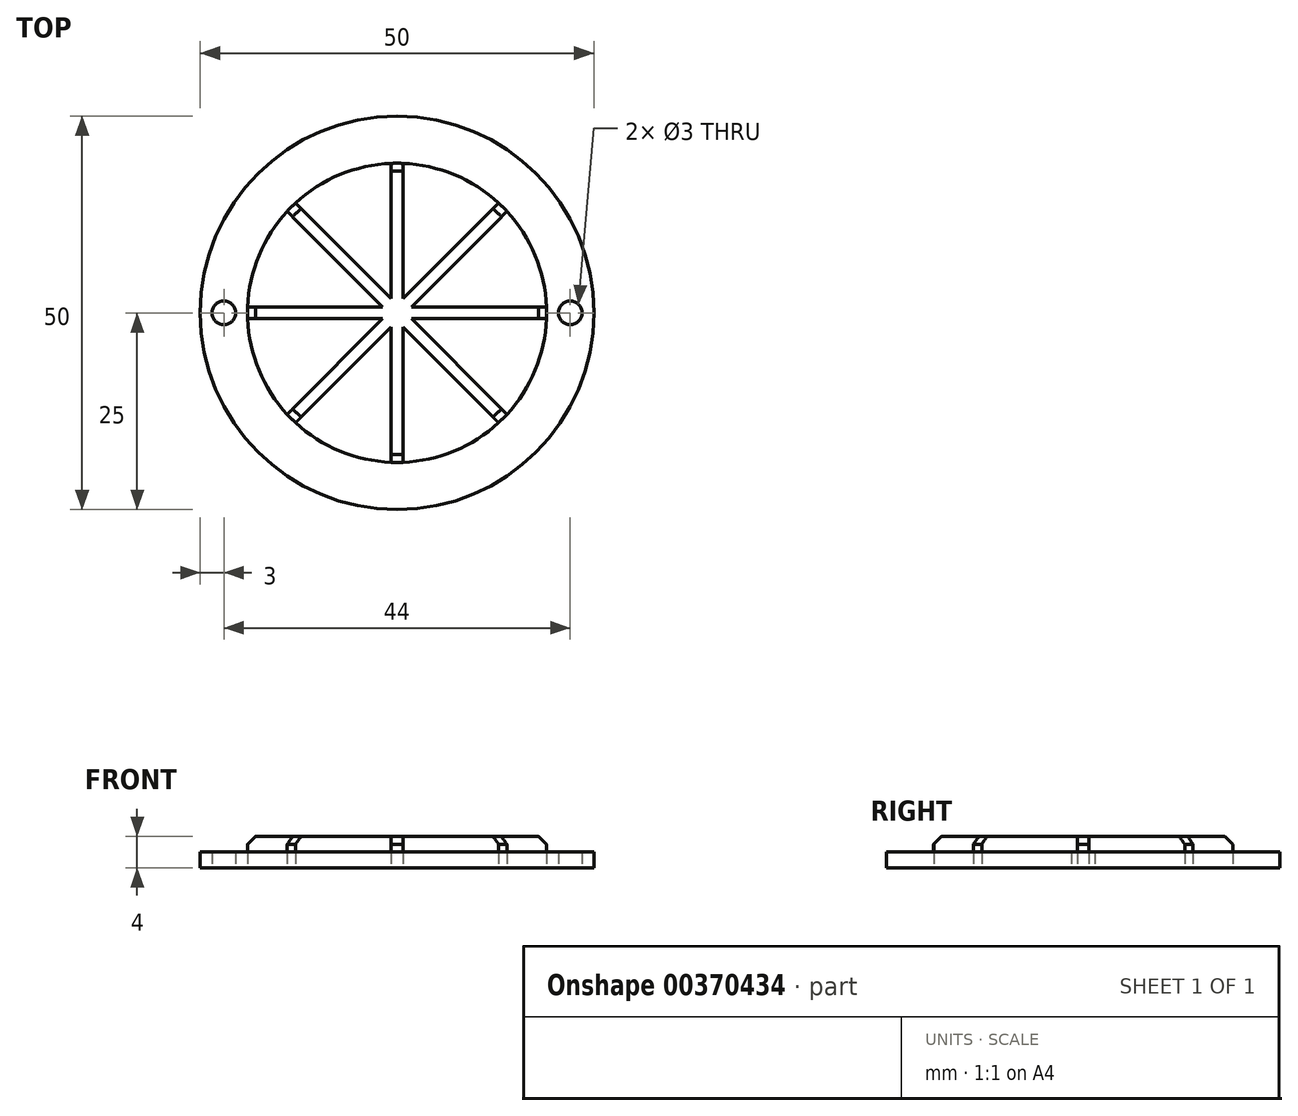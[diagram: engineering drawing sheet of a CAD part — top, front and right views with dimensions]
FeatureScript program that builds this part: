
annotation { "Feature Type Name" : "Feature", "Feature Type Description" : "" }
export const myFeature = defineFeature(function(context is Context, id is Id, definition is map)
    precondition{}
    {
        {
            var Q0;
            Q0=qCreatedBy(makeId("Top.planeOp"),FACE);
            var sketch = newSketch(context, id + "F0", { "sketchPlane" : qUnion([Q0])});
            skCircle(sketch, "E0", {"center": v(0, 0) * mm, "radius": 19 * mm});
            skCircle(sketch, "E1", {"center": v(0, 0) * mm, "radius": 25 * mm});
            skLineSegment(sketch, "E2", {"start": v(0, 0) * mm, "end": v(-19, 0) * mm});
            skLineSegment(sketch, "E3", {"start": v(0, 0) * mm, "end": v(19, 0) * mm});
            skLineSegment(sketch, "E4", {"start": v(0, 0) * mm, "end": v(0, 19) * mm});
            skLineSegment(sketch, "E5", {"start": v(0, 0) * mm, "end": v(0, -19) * mm});
            skPoint(sketch, "E6", {"position": v(-22, 0) * mm});
            skPoint(sketch, "E7", {"position": v(22, 0) * mm});
            skLineSegment(sketch, "E8", {"start": v(-18.99, 0.75) * mm, "end": v(18.99, 0.75) * mm});
            skLineSegment(sketch, "E9", {"start": v(-18.99, -0.75) * mm, "end": v(18.99, -0.75) * mm});
            skLineSegment(sketch, "E10", {"start": v(-0.75, 18.99) * mm, "end": v(-0.75, -18.99) * mm});
            skLineSegment(sketch, "E11", {"start": v(0.75, 18.99) * mm, "end": v(0.75, -18.99) * mm});
            skLineSegment(sketch, "E12", {"start": v(0, 0) * mm, "end": v(13.44, -13.44) * mm});
            skLineSegment(sketch, "E13", {"start": v(0, 0) * mm, "end": v(-13.44, 13.44) * mm});
            skLineSegment(sketch, "E14", {"start": v(0, 0) * mm, "end": v(13.44, 13.44) * mm});
            skLineSegment(sketch, "E15", {"start": v(0, 0) * mm, "end": v(-13.44, -13.44) * mm});
            skLineSegment(sketch, "E16", {"start": v(-12.9, -13.95) * mm, "end": v(13.95, 12.9) * mm});
            skLineSegment(sketch, "E17", {"start": v(-13.95, -12.9) * mm, "end": v(12.9, 13.95) * mm});
            skLineSegment(sketch, "E18", {"start": v(-12.9, 13.95) * mm, "end": v(13.95, -12.9) * mm});
            skLineSegment(sketch, "E19", {"start": v(-13.95, 12.9) * mm, "end": v(12.9, -13.95) * mm});
            skSolve(sketch);
        }
        {
            var Q0;
            {var subQ0=sQuery(id+"F0.wireOp",EDGE,"E2");var subQ1=sQuery(id+"F0.wireOp",EDGE,"E0");var subQ2=makeQuery(id+"F0.imprint","INTERSECT",VERTEX,{"derivedFrom":[subQ1,subQ0]});Q0=makeQuery(id+"F0.imprint","IMPRINT",FACE,{"disambiguationData":[TD([[makeQuery(id+"F0.imprint","IMPRINT",EDGE,{"disambiguationData":[TD([[subQ2,-1.0]])],"derivedFrom":subQ1}),1.0]])]});}
            var Q1;
            {var subQ0=sQuery(id+"F0.wireOp",EDGE,"E2");var subQ1=sQuery(id+"F0.wireOp",EDGE,"E0");var subQ2=makeQuery(id+"F0.imprint","INTERSECT",VERTEX,{"derivedFrom":[subQ1,subQ0]});Q1=makeQuery(id+"F0.imprint","IMPRINT",FACE,{"disambiguationData":[TD([[makeQuery(id+"F0.imprint","IMPRINT",EDGE,{"disambiguationData":[TD([[subQ2,1.0]])],"derivedFrom":subQ1}),1.0]])]});}
            var Q2;
            {var subQ0=sQuery(id+"F0.wireOp",EDGE,"E13");var subQ1=sQuery(id+"F0.wireOp",EDGE,"E0");var subQ2=makeQuery(id+"F0.imprint","INTERSECT",VERTEX,{"derivedFrom":[subQ1,subQ0]});Q2=makeQuery(id+"F0.imprint","IMPRINT",FACE,{"disambiguationData":[TD([[makeQuery(id+"F0.imprint","IMPRINT",EDGE,{"disambiguationData":[TD([[subQ2,-1.0]])],"derivedFrom":subQ1}),1.0]])]});}
            var Q3;
            {var subQ0=sQuery(id+"F0.wireOp",EDGE,"E13");var subQ1=sQuery(id+"F0.wireOp",EDGE,"E0");var subQ2=makeQuery(id+"F0.imprint","INTERSECT",VERTEX,{"derivedFrom":[subQ1,subQ0]});Q3=makeQuery(id+"F0.imprint","IMPRINT",FACE,{"disambiguationData":[TD([[makeQuery(id+"F0.imprint","IMPRINT",EDGE,{"disambiguationData":[TD([[subQ2,1.0]])],"derivedFrom":subQ1}),1.0]])]});}
            var Q4;
            {var subQ0=sQuery(id+"F0.wireOp",EDGE,"E4");var subQ1=sQuery(id+"F0.wireOp",EDGE,"E0");var subQ2=makeQuery(id+"F0.imprint","INTERSECT",VERTEX,{"derivedFrom":[subQ1,subQ0]});Q4=makeQuery(id+"F0.imprint","IMPRINT",FACE,{"disambiguationData":[TD([[makeQuery(id+"F0.imprint","IMPRINT",EDGE,{"disambiguationData":[TD([[subQ2,-1.0]])],"derivedFrom":subQ1}),1.0]])]});}
            var Q5;
            {var subQ0=sQuery(id+"F0.wireOp",EDGE,"E4");var subQ1=sQuery(id+"F0.wireOp",EDGE,"E0");var subQ2=makeQuery(id+"F0.imprint","INTERSECT",VERTEX,{"derivedFrom":[subQ1,subQ0]});Q5=makeQuery(id+"F0.imprint","IMPRINT",FACE,{"disambiguationData":[TD([[makeQuery(id+"F0.imprint","IMPRINT",EDGE,{"disambiguationData":[TD([[subQ2,1.0]])],"derivedFrom":subQ1}),1.0]])]});}
            var Q6;
            {var subQ0=sQuery(id+"F0.wireOp",EDGE,"E14");var subQ1=sQuery(id+"F0.wireOp",EDGE,"E0");var subQ2=makeQuery(id+"F0.imprint","INTERSECT",VERTEX,{"derivedFrom":[subQ1,subQ0]});Q6=makeQuery(id+"F0.imprint","IMPRINT",FACE,{"disambiguationData":[TD([[makeQuery(id+"F0.imprint","IMPRINT",EDGE,{"disambiguationData":[TD([[subQ2,-1.0]])],"derivedFrom":subQ1}),1.0]])]});}
            var Q7;
            {var subQ0=sQuery(id+"F0.wireOp",EDGE,"E14");var subQ1=sQuery(id+"F0.wireOp",EDGE,"E0");var subQ2=makeQuery(id+"F0.imprint","INTERSECT",VERTEX,{"derivedFrom":[subQ1,subQ0]});Q7=makeQuery(id+"F0.imprint","IMPRINT",FACE,{"disambiguationData":[TD([[makeQuery(id+"F0.imprint","IMPRINT",EDGE,{"disambiguationData":[TD([[subQ2,1.0]])],"derivedFrom":subQ1}),1.0]])]});}
            var Q8;
            {var subQ0=sQuery(id+"F0.wireOp",EDGE,"E3");var subQ1=sQuery(id+"F0.wireOp",EDGE,"E0");var subQ2=makeQuery(id+"F0.imprint","INTERSECT",VERTEX,{"derivedFrom":[subQ1,subQ0]});Q8=makeQuery(id+"F0.imprint","IMPRINT",FACE,{"disambiguationData":[TD([[makeQuery(id+"F0.imprint","IMPRINT",EDGE,{"disambiguationData":[TD([[subQ2,-1.0]])],"derivedFrom":subQ1}),1.0]])]});}
            var Q9;
            {var subQ0=sQuery(id+"F0.wireOp",EDGE,"E3");var subQ1=sQuery(id+"F0.wireOp",EDGE,"E0");var subQ2=makeQuery(id+"F0.imprint","INTERSECT",VERTEX,{"derivedFrom":[subQ1,subQ0]});Q9=makeQuery(id+"F0.imprint","IMPRINT",FACE,{"disambiguationData":[TD([[makeQuery(id+"F0.imprint","IMPRINT",EDGE,{"disambiguationData":[TD([[subQ2,1.0]])],"derivedFrom":subQ1}),1.0]])]});}
            var Q10;
            {var subQ0=sQuery(id+"F0.wireOp",EDGE,"E12");var subQ1=sQuery(id+"F0.wireOp",EDGE,"E0");var subQ2=makeQuery(id+"F0.imprint","INTERSECT",VERTEX,{"derivedFrom":[subQ1,subQ0]});Q10=makeQuery(id+"F0.imprint","IMPRINT",FACE,{"disambiguationData":[TD([[makeQuery(id+"F0.imprint","IMPRINT",EDGE,{"disambiguationData":[TD([[subQ2,-1.0]])],"derivedFrom":subQ1}),1.0]])]});}
            var Q11;
            {var subQ0=sQuery(id+"F0.wireOp",EDGE,"E12");var subQ1=sQuery(id+"F0.wireOp",EDGE,"E0");var subQ2=makeQuery(id+"F0.imprint","INTERSECT",VERTEX,{"derivedFrom":[subQ1,subQ0]});Q11=makeQuery(id+"F0.imprint","IMPRINT",FACE,{"disambiguationData":[TD([[makeQuery(id+"F0.imprint","IMPRINT",EDGE,{"disambiguationData":[TD([[subQ2,1.0]])],"derivedFrom":subQ1}),1.0]])]});}
            var Q12;
            {var subQ0=sQuery(id+"F0.wireOp",EDGE,"E5");var subQ1=sQuery(id+"F0.wireOp",EDGE,"E0");var subQ2=makeQuery(id+"F0.imprint","INTERSECT",VERTEX,{"derivedFrom":[subQ1,subQ0]});Q12=makeQuery(id+"F0.imprint","IMPRINT",FACE,{"disambiguationData":[TD([[makeQuery(id+"F0.imprint","IMPRINT",EDGE,{"disambiguationData":[TD([[subQ2,-1.0]])],"derivedFrom":subQ1}),1.0]])]});}
            var Q13;
            {var subQ0=sQuery(id+"F0.wireOp",EDGE,"E5");var subQ1=sQuery(id+"F0.wireOp",EDGE,"E0");var subQ2=makeQuery(id+"F0.imprint","INTERSECT",VERTEX,{"derivedFrom":[subQ1,subQ0]});Q13=makeQuery(id+"F0.imprint","IMPRINT",FACE,{"disambiguationData":[TD([[makeQuery(id+"F0.imprint","IMPRINT",EDGE,{"disambiguationData":[TD([[subQ2,1.0]])],"derivedFrom":subQ1}),1.0]])]});}
            var Q14;
            {var subQ0=sQuery(id+"F0.wireOp",EDGE,"E15");var subQ1=sQuery(id+"F0.wireOp",EDGE,"E0");var subQ2=makeQuery(id+"F0.imprint","INTERSECT",VERTEX,{"derivedFrom":[subQ1,subQ0]});Q14=makeQuery(id+"F0.imprint","IMPRINT",FACE,{"disambiguationData":[TD([[makeQuery(id+"F0.imprint","IMPRINT",EDGE,{"disambiguationData":[TD([[subQ2,-1.0]])],"derivedFrom":subQ1}),1.0]])]});}
            var Q15;
            {var subQ0=sQuery(id+"F0.wireOp",EDGE,"E15");var subQ1=sQuery(id+"F0.wireOp",EDGE,"E0");var subQ2=makeQuery(id+"F0.imprint","INTERSECT",VERTEX,{"derivedFrom":[subQ1,subQ0]});Q15=makeQuery(id+"F0.imprint","IMPRINT",FACE,{"disambiguationData":[TD([[makeQuery(id+"F0.imprint","IMPRINT",EDGE,{"disambiguationData":[TD([[subQ2,1.0]])],"derivedFrom":subQ1}),1.0]])]});}
            var Q16;
            {var subQ0=sQuery(id+"F0.wireOp",EDGE,"E17");var subQ1=sQuery(id+"F0.wireOp",EDGE,"E9");var subQ2=makeQuery(id+"F0.imprint","INTERSECT",VERTEX,{"derivedFrom":[subQ1,subQ0]});Q16=makeQuery(id+"F0.imprint","IMPRINT",FACE,{"disambiguationData":[TD([[makeQuery(id+"F0.imprint","IMPRINT",EDGE,{"disambiguationData":[TD([[subQ2,-1.0]])],"derivedFrom":subQ1}),1.0]])]});}
            var Q17;
            {var subQ0=sQuery(id+"F0.wireOp",EDGE,"E19");var subQ1=sQuery(id+"F0.wireOp",EDGE,"E9");var subQ2=makeQuery(id+"F0.imprint","INTERSECT",VERTEX,{"derivedFrom":[subQ1,subQ0]});Q17=makeQuery(id+"F0.imprint","IMPRINT",FACE,{"disambiguationData":[TD([[makeQuery(id+"F0.imprint","IMPRINT",EDGE,{"disambiguationData":[TD([[subQ2,1.0]])],"derivedFrom":subQ1}),-1.0]])]});}
            var Q18;
            {var subQ0=sQuery(id+"F0.wireOp",EDGE,"E16");var subQ1=sQuery(id+"F0.wireOp",EDGE,"E9");var subQ2=makeQuery(id+"F0.imprint","INTERSECT",VERTEX,{"derivedFrom":[subQ1,subQ0]});Q18=makeQuery(id+"F0.imprint","IMPRINT",FACE,{"disambiguationData":[TD([[makeQuery(id+"F0.imprint","IMPRINT",EDGE,{"disambiguationData":[TD([[subQ2,-1.0]])],"derivedFrom":subQ1}),-1.0]])]});}
            var Q19;
            {var subQ0=sQuery(id+"F0.wireOp",EDGE,"E18");var subQ1=sQuery(id+"F0.wireOp",EDGE,"E9");var subQ2=makeQuery(id+"F0.imprint","INTERSECT",VERTEX,{"derivedFrom":[subQ1,subQ0]});Q19=makeQuery(id+"F0.imprint","IMPRINT",FACE,{"disambiguationData":[TD([[makeQuery(id+"F0.imprint","IMPRINT",EDGE,{"disambiguationData":[TD([[subQ2,1.0]])],"derivedFrom":subQ1}),1.0]])]});}
            var Q20;
            {var subQ0=sQuery(id+"F0.wireOp",EDGE,"E16");var subQ1=sQuery(id+"F0.wireOp",EDGE,"E11");var subQ2=makeQuery(id+"F0.imprint","INTERSECT",VERTEX,{"derivedFrom":[subQ1,subQ0]});Q20=makeQuery(id+"F0.imprint","IMPRINT",FACE,{"disambiguationData":[TD([[makeQuery(id+"F0.imprint","IMPRINT",EDGE,{"disambiguationData":[TD([[subQ2,1.0]])],"derivedFrom":subQ0}),-1.0]])]});}
            var Q21;
            {var subQ0=sQuery(id+"F0.wireOp",EDGE,"E16");var subQ1=sQuery(id+"F0.wireOp",EDGE,"E9");var subQ2=makeQuery(id+"F0.imprint","INTERSECT",VERTEX,{"derivedFrom":[subQ1,subQ0]});Q21=makeQuery(id+"F0.imprint","IMPRINT",FACE,{"disambiguationData":[TD([[makeQuery(id+"F0.imprint","IMPRINT",EDGE,{"disambiguationData":[TD([[subQ2,-1.0]])],"derivedFrom":subQ0}),-1.0]])]});}
            var Q22;
            {var subQ0=sQuery(id+"F0.wireOp",EDGE,"E9");var subQ1=sQuery(id+"F0.wireOp",EDGE,"E5");var subQ2=makeQuery(id+"F0.imprint","INTERSECT",VERTEX,{"derivedFrom":[subQ1,subQ0]});Q22=makeQuery(id+"F0.imprint","IMPRINT",FACE,{"disambiguationData":[TD([[makeQuery(id+"F0.imprint","IMPRINT",EDGE,{"disambiguationData":[TD([[subQ2,-1.0]])],"derivedFrom":subQ0}),-1.0]])]});}
            var Q23;
            {var subQ0=sQuery(id+"F0.wireOp",EDGE,"E9");var subQ1=sQuery(id+"F0.wireOp",EDGE,"E5");var subQ2=makeQuery(id+"F0.imprint","INTERSECT",VERTEX,{"derivedFrom":[subQ1,subQ0]});Q23=makeQuery(id+"F0.imprint","IMPRINT",FACE,{"disambiguationData":[TD([[makeQuery(id+"F0.imprint","IMPRINT",EDGE,{"disambiguationData":[TD([[subQ2,1.0]])],"derivedFrom":subQ0}),-1.0]])]});}
            var Q24;
            {var subQ1=sQuery(id+"F0.wireOp",EDGE,"E5");var subQ3=sQuery(id+"F0.wireOp",EDGE,"E9");var subQ4=makeQuery(id+"F0.imprint","INTERSECT",VERTEX,{"derivedFrom":[subQ1,subQ3]});Q24=makeQuery(id+"F0.imprint","IMPRINT",FACE,{"disambiguationData":[TD([[makeQuery(id+"F0.imprint","IMPRINT",EDGE,{"disambiguationData":[TD([[subQ4,1.0]])],"derivedFrom":subQ3}),1.0]])]});}
            var Q25;
            {var subQ0=sQuery(id+"F0.wireOp",EDGE,"E19");var subQ1=sQuery(id+"F0.wireOp",EDGE,"E9");var subQ2=makeQuery(id+"F0.imprint","INTERSECT",VERTEX,{"derivedFrom":[subQ1,subQ0]});Q25=makeQuery(id+"F0.imprint","IMPRINT",FACE,{"disambiguationData":[TD([[makeQuery(id+"F0.imprint","IMPRINT",EDGE,{"disambiguationData":[TD([[subQ2,1.0]])],"derivedFrom":subQ0}),-1.0]])]});}
            var Q26;
            {var subQ0=sQuery(id+"F0.wireOp",EDGE,"E19");var subQ1=sQuery(id+"F0.wireOp",EDGE,"E10");var subQ2=makeQuery(id+"F0.imprint","INTERSECT",VERTEX,{"derivedFrom":[subQ1,subQ0]});Q26=makeQuery(id+"F0.imprint","IMPRINT",FACE,{"disambiguationData":[TD([[makeQuery(id+"F0.imprint","IMPRINT",EDGE,{"disambiguationData":[TD([[subQ2,-1.0]])],"derivedFrom":subQ0}),-1.0]])]});}
            var Q27;
            {var subQ1=sQuery(id+"F0.wireOp",EDGE,"E2");var subQ3=sQuery(id+"F0.wireOp",EDGE,"E10");var subQ4=makeQuery(id+"F0.imprint","INTERSECT",VERTEX,{"derivedFrom":[subQ1,subQ3]});Q27=makeQuery(id+"F0.imprint","IMPRINT",FACE,{"disambiguationData":[TD([[makeQuery(id+"F0.imprint","IMPRINT",EDGE,{"disambiguationData":[TD([[subQ4,-1.0]])],"derivedFrom":subQ3}),1.0]])]});}
            var Q28;
            {var subQ0=sQuery(id+"F0.wireOp",EDGE,"E10");var subQ1=sQuery(id+"F0.wireOp",EDGE,"E2");var subQ2=makeQuery(id+"F0.imprint","INTERSECT",VERTEX,{"derivedFrom":[subQ1,subQ0]});Q28=makeQuery(id+"F0.imprint","IMPRINT",FACE,{"disambiguationData":[TD([[makeQuery(id+"F0.imprint","IMPRINT",EDGE,{"disambiguationData":[TD([[subQ2,-1.0]])],"derivedFrom":subQ0}),-1.0]])]});}
            var Q29;
            {var subQ0=sQuery(id+"F0.wireOp",EDGE,"E10");var subQ1=sQuery(id+"F0.wireOp",EDGE,"E2");var subQ2=makeQuery(id+"F0.imprint","INTERSECT",VERTEX,{"derivedFrom":[subQ1,subQ0]});Q29=makeQuery(id+"F0.imprint","IMPRINT",FACE,{"disambiguationData":[TD([[makeQuery(id+"F0.imprint","IMPRINT",EDGE,{"disambiguationData":[TD([[subQ2,1.0]])],"derivedFrom":subQ0}),-1.0]])]});}
            var Q30;
            {var subQ0=sQuery(id+"F0.wireOp",EDGE,"E19");var subQ1=sQuery(id+"F0.wireOp",EDGE,"E8");var subQ2=makeQuery(id+"F0.imprint","INTERSECT",VERTEX,{"derivedFrom":[subQ1,subQ0]});Q30=makeQuery(id+"F0.imprint","IMPRINT",FACE,{"disambiguationData":[TD([[makeQuery(id+"F0.imprint","IMPRINT",EDGE,{"disambiguationData":[TD([[subQ2,-1.0]])],"derivedFrom":subQ1}),-1.0]])]});}
            var Q31;
            {var subQ1=sQuery(id+"F0.wireOp",EDGE,"E2");var subQ3=sQuery(id+"F0.wireOp",EDGE,"E10");var subQ4=makeQuery(id+"F0.imprint","INTERSECT",VERTEX,{"derivedFrom":[subQ1,subQ3]});Q31=makeQuery(id+"F0.imprint","IMPRINT",FACE,{"disambiguationData":[TD([[makeQuery(id+"F0.imprint","IMPRINT",EDGE,{"disambiguationData":[TD([[subQ4,1.0]])],"derivedFrom":subQ3}),1.0]])]});}
            var Q32;
            {var subQ0=sQuery(id+"F0.wireOp",EDGE,"E17");var subQ1=sQuery(id+"F0.wireOp",EDGE,"E10");var subQ2=makeQuery(id+"F0.imprint","INTERSECT",VERTEX,{"derivedFrom":[subQ1,subQ0]});Q32=makeQuery(id+"F0.imprint","IMPRINT",FACE,{"disambiguationData":[TD([[makeQuery(id+"F0.imprint","IMPRINT",EDGE,{"disambiguationData":[TD([[subQ2,-1.0]])],"derivedFrom":subQ0}),1.0]])]});}
            var Q33;
            {var subQ0=sQuery(id+"F0.wireOp",EDGE,"E17");var subQ1=sQuery(id+"F0.wireOp",EDGE,"E8");var subQ2=makeQuery(id+"F0.imprint","INTERSECT",VERTEX,{"derivedFrom":[subQ1,subQ0]});Q33=makeQuery(id+"F0.imprint","IMPRINT",FACE,{"disambiguationData":[TD([[makeQuery(id+"F0.imprint","IMPRINT",EDGE,{"disambiguationData":[TD([[subQ2,1.0]])],"derivedFrom":subQ1}),1.0]])]});}
            var Q34;
            {var subQ0=sQuery(id+"F0.wireOp",EDGE,"E17");var subQ1=sQuery(id+"F0.wireOp",EDGE,"E8");var subQ2=makeQuery(id+"F0.imprint","INTERSECT",VERTEX,{"derivedFrom":[subQ1,subQ0]});Q34=makeQuery(id+"F0.imprint","IMPRINT",FACE,{"disambiguationData":[TD([[makeQuery(id+"F0.imprint","IMPRINT",EDGE,{"disambiguationData":[TD([[subQ2,1.0]])],"derivedFrom":subQ0}),1.0]])]});}
            var Q35;
            {var subQ1=sQuery(id+"F0.wireOp",EDGE,"E4");var subQ3=sQuery(id+"F0.wireOp",EDGE,"E8");var subQ4=makeQuery(id+"F0.imprint","INTERSECT",VERTEX,{"derivedFrom":[subQ1,subQ3]});Q35=makeQuery(id+"F0.imprint","IMPRINT",FACE,{"disambiguationData":[TD([[makeQuery(id+"F0.imprint","IMPRINT",EDGE,{"disambiguationData":[TD([[subQ4,1.0]])],"derivedFrom":subQ3}),-1.0]])]});}
            var Q36;
            {var subQ0=sQuery(id+"F0.wireOp",EDGE,"E8");var subQ1=sQuery(id+"F0.wireOp",EDGE,"E4");var subQ2=makeQuery(id+"F0.imprint","INTERSECT",VERTEX,{"derivedFrom":[subQ1,subQ0]});Q36=makeQuery(id+"F0.imprint","IMPRINT",FACE,{"disambiguationData":[TD([[makeQuery(id+"F0.imprint","IMPRINT",EDGE,{"disambiguationData":[TD([[subQ2,1.0]])],"derivedFrom":subQ0}),1.0]])]});}
            var Q37;
            {var subQ0=sQuery(id+"F0.wireOp",EDGE,"E18");var subQ1=sQuery(id+"F0.wireOp",EDGE,"E8");var subQ2=makeQuery(id+"F0.imprint","INTERSECT",VERTEX,{"derivedFrom":[subQ1,subQ0]});Q37=makeQuery(id+"F0.imprint","IMPRINT",FACE,{"disambiguationData":[TD([[makeQuery(id+"F0.imprint","IMPRINT",EDGE,{"disambiguationData":[TD([[subQ2,-1.0]])],"derivedFrom":subQ1}),1.0]])]});}
            var Q38;
            {var subQ0=sQuery(id+"F0.wireOp",EDGE,"E8");var subQ1=sQuery(id+"F0.wireOp",EDGE,"E4");var subQ2=makeQuery(id+"F0.imprint","INTERSECT",VERTEX,{"derivedFrom":[subQ1,subQ0]});Q38=makeQuery(id+"F0.imprint","IMPRINT",FACE,{"disambiguationData":[TD([[makeQuery(id+"F0.imprint","IMPRINT",EDGE,{"disambiguationData":[TD([[subQ2,-1.0]])],"derivedFrom":subQ0}),1.0]])]});}
            var Q39;
            {var subQ0=sQuery(id+"F0.wireOp",EDGE,"E18");var subQ1=sQuery(id+"F0.wireOp",EDGE,"E8");var subQ2=makeQuery(id+"F0.imprint","INTERSECT",VERTEX,{"derivedFrom":[subQ1,subQ0]});Q39=makeQuery(id+"F0.imprint","IMPRINT",FACE,{"disambiguationData":[TD([[makeQuery(id+"F0.imprint","IMPRINT",EDGE,{"disambiguationData":[TD([[subQ2,-1.0]])],"derivedFrom":subQ0}),1.0]])]});}
            var Q40;
            {var subQ0=sQuery(id+"F0.wireOp",EDGE,"E18");var subQ1=sQuery(id+"F0.wireOp",EDGE,"E11");var subQ2=makeQuery(id+"F0.imprint","INTERSECT",VERTEX,{"derivedFrom":[subQ1,subQ0]});Q40=makeQuery(id+"F0.imprint","IMPRINT",FACE,{"disambiguationData":[TD([[makeQuery(id+"F0.imprint","IMPRINT",EDGE,{"disambiguationData":[TD([[subQ2,1.0]])],"derivedFrom":subQ0}),1.0]])]});}
            var Q41;
            {var subQ0=sQuery(id+"F0.wireOp",EDGE,"E16");var subQ1=sQuery(id+"F0.wireOp",EDGE,"E8");var subQ2=makeQuery(id+"F0.imprint","INTERSECT",VERTEX,{"derivedFrom":[subQ1,subQ0]});Q41=makeQuery(id+"F0.imprint","IMPRINT",FACE,{"disambiguationData":[TD([[makeQuery(id+"F0.imprint","IMPRINT",EDGE,{"disambiguationData":[TD([[subQ2,1.0]])],"derivedFrom":subQ1}),-1.0]])]});}
            var Q42;
            {var subQ0=sQuery(id+"F0.wireOp",EDGE,"E11");var subQ1=sQuery(id+"F0.wireOp",EDGE,"E3");var subQ2=makeQuery(id+"F0.imprint","INTERSECT",VERTEX,{"derivedFrom":[subQ1,subQ0]});Q42=makeQuery(id+"F0.imprint","IMPRINT",FACE,{"disambiguationData":[TD([[makeQuery(id+"F0.imprint","IMPRINT",EDGE,{"disambiguationData":[TD([[subQ2,1.0]])],"derivedFrom":subQ0}),1.0]])]});}
            var Q43;
            {var subQ1=sQuery(id+"F0.wireOp",EDGE,"E3");var subQ3=sQuery(id+"F0.wireOp",EDGE,"E11");var subQ4=makeQuery(id+"F0.imprint","INTERSECT",VERTEX,{"derivedFrom":[subQ1,subQ3]});Q43=makeQuery(id+"F0.imprint","IMPRINT",FACE,{"disambiguationData":[TD([[makeQuery(id+"F0.imprint","IMPRINT",EDGE,{"disambiguationData":[TD([[subQ4,-1.0]])],"derivedFrom":subQ3}),-1.0]])]});}
            var Q44;
            {var subQ1=sQuery(id+"F0.wireOp",EDGE,"E5");var subQ3=sQuery(id+"F0.wireOp",EDGE,"E9");var subQ4=makeQuery(id+"F0.imprint","INTERSECT",VERTEX,{"derivedFrom":[subQ1,subQ3]});Q44=makeQuery(id+"F0.imprint","IMPRINT",FACE,{"disambiguationData":[TD([[makeQuery(id+"F0.imprint","IMPRINT",EDGE,{"disambiguationData":[TD([[subQ4,-1.0]])],"derivedFrom":subQ3}),1.0]])]});}
            var Q45;
            {var subQ1=sQuery(id+"F0.wireOp",EDGE,"E3");var subQ3=sQuery(id+"F0.wireOp",EDGE,"E11");var subQ4=makeQuery(id+"F0.imprint","INTERSECT",VERTEX,{"derivedFrom":[subQ1,subQ3]});Q45=makeQuery(id+"F0.imprint","IMPRINT",FACE,{"disambiguationData":[TD([[makeQuery(id+"F0.imprint","IMPRINT",EDGE,{"disambiguationData":[TD([[subQ4,1.0]])],"derivedFrom":subQ3}),-1.0]])]});}
            var Q46;
            {var subQ1=sQuery(id+"F0.wireOp",EDGE,"E4");var subQ3=sQuery(id+"F0.wireOp",EDGE,"E8");var subQ4=makeQuery(id+"F0.imprint","INTERSECT",VERTEX,{"derivedFrom":[subQ1,subQ3]});Q46=makeQuery(id+"F0.imprint","IMPRINT",FACE,{"disambiguationData":[TD([[makeQuery(id+"F0.imprint","IMPRINT",EDGE,{"disambiguationData":[TD([[subQ4,-1.0]])],"derivedFrom":subQ3}),-1.0]])]});}
            var Q47;
            {var subQ0=sQuery(id+"F0.wireOp",EDGE,"E11");var subQ1=sQuery(id+"F0.wireOp",EDGE,"E3");var subQ2=makeQuery(id+"F0.imprint","INTERSECT",VERTEX,{"derivedFrom":[subQ1,subQ0]});Q47=makeQuery(id+"F0.imprint","IMPRINT",FACE,{"disambiguationData":[TD([[makeQuery(id+"F0.imprint","IMPRINT",EDGE,{"disambiguationData":[TD([[subQ2,-1.0]])],"derivedFrom":subQ0}),1.0]])]});}
            extrude(context, id + "F1", {"entities" : qUnion([Q0, Q1, Q2, Q3, Q4, Q5, Q6, Q7, Q8, Q9, Q10, Q11, Q12, Q13, Q14, Q15, Q16, Q17, Q18, Q19, Q20, Q21, Q22, Q23, Q24, Q25, Q26, Q27, Q28, Q29, Q30, Q31, Q32, Q33, Q34, Q35, Q36, Q37, Q38, Q39, Q40, Q41, Q42, Q43, Q44, Q45, Q46, Q47]), "depth" : 4 * mm});
        }
        {
            var Q0;
            Q0=makeQuery(id+"F0.imprint","IMPRINT",FACE,{"disambiguationData":[TD([[makeQuery(id+"F0.imprint","IMPRINT",EDGE,{"derivedFrom":sQuery(id+"F0.wireOp",EDGE,"E1")}),1.0]])]});
            extrude(context, id + "F2", {"entities" : qUnion([Q0]), "operationType" : NewBodyOperationType.ADD, "depth" : 2 * mm});
        }
        {
            var Q0;
            Q0=sQuery(id+"F0.wireOp",VERTEX,"E6");
            var Q1;
            Q1=sQuery(id+"F0.wireOp",VERTEX,"E7");
            var Q2;
            Q2=makeQuery(id+"F1.opExtrude","SWEPT_BODY",BODY,{"disambiguationData":[OSD([sQuery(id+"F0.wireOp",EDGE,"E0"),sQuery(id+"F0.wireOp",EDGE,"E1"),sQuery(id+"F0.wireOp",EDGE,"E8"),sQuery(id+"F0.wireOp",EDGE,"E9"),sQuery(id+"F0.wireOp",EDGE,"E10"),sQuery(id+"F0.wireOp",EDGE,"E11"),sQuery(id+"F0.wireOp",EDGE,"E16"),sQuery(id+"F0.wireOp",EDGE,"E17"),sQuery(id+"F0.wireOp",EDGE,"E18"),sQuery(id+"F0.wireOp",EDGE,"E19")])]});
            hole(context, id + "F3", {"style" : HoleStyle.SIMPLE, "endStyle" : HoleEndStyle.THROUGH, "oppositeDirection" : true, "holeDiameter" : 3 * mm, "isTappedThrough" : true, "tappedDepth" : 12 * mm, "tapClearance" : 3, "locations" : qUnion([Q0, Q1]), "scope" : qUnion([Q2])});
        }
        {
            var Q0;
            {var subQ0=sQuery(id+"F0.wireOp",EDGE,"E0");var subQ1=makeQuery(id+"F0.imprint","INTERSECT",VERTEX,{"derivedFrom":[subQ0,sQuery(id+"F0.wireOp",EDGE,"E2")]});Q0=makeQuery(id+"F1.opExtrude","CAP_EDGE",EDGE,{"disambiguationData":[OSD([subQ0]),TDD([makeQuery(id+"F0.imprint","IMPRINT",EDGE,{"disambiguationData":[TD([[subQ1,1.0]])],"derivedFrom":subQ0}),makeQuery(id+"F0.imprint","IMPRINT",EDGE,{"disambiguationData":[TD([[subQ1,-1.0]])],"derivedFrom":subQ0})])],"isStart":false});}
            var Q1;
            {var subQ0=sQuery(id+"F0.wireOp",EDGE,"E0");var subQ1=makeQuery(id+"F0.imprint","INTERSECT",VERTEX,{"derivedFrom":[subQ0,sQuery(id+"F0.wireOp",EDGE,"E15")]});Q1=makeQuery(id+"F1.opExtrude","CAP_EDGE",EDGE,{"disambiguationData":[OSD([subQ0]),TDD([makeQuery(id+"F0.imprint","IMPRINT",EDGE,{"disambiguationData":[TD([[subQ1,1.0]])],"derivedFrom":subQ0}),makeQuery(id+"F0.imprint","IMPRINT",EDGE,{"disambiguationData":[TD([[subQ1,-1.0]])],"derivedFrom":subQ0})])],"isStart":false});}
            var Q2;
            {var subQ0=sQuery(id+"F0.wireOp",EDGE,"E0");var subQ1=makeQuery(id+"F0.imprint","INTERSECT",VERTEX,{"derivedFrom":[subQ0,sQuery(id+"F0.wireOp",EDGE,"E5")]});Q2=makeQuery(id+"F1.opExtrude","CAP_EDGE",EDGE,{"disambiguationData":[OSD([subQ0]),TDD([makeQuery(id+"F0.imprint","IMPRINT",EDGE,{"disambiguationData":[TD([[subQ1,1.0]])],"derivedFrom":subQ0}),makeQuery(id+"F0.imprint","IMPRINT",EDGE,{"disambiguationData":[TD([[subQ1,-1.0]])],"derivedFrom":subQ0})])],"isStart":false});}
            var Q3;
            {var subQ0=sQuery(id+"F0.wireOp",EDGE,"E0");var subQ1=makeQuery(id+"F0.imprint","INTERSECT",VERTEX,{"derivedFrom":[subQ0,sQuery(id+"F0.wireOp",EDGE,"E12")]});Q3=makeQuery(id+"F1.opExtrude","CAP_EDGE",EDGE,{"disambiguationData":[OSD([subQ0]),TDD([makeQuery(id+"F0.imprint","IMPRINT",EDGE,{"disambiguationData":[TD([[subQ1,1.0]])],"derivedFrom":subQ0}),makeQuery(id+"F0.imprint","IMPRINT",EDGE,{"disambiguationData":[TD([[subQ1,-1.0]])],"derivedFrom":subQ0})])],"isStart":false});}
            var Q4;
            {var subQ0=sQuery(id+"F0.wireOp",EDGE,"E0");var subQ1=makeQuery(id+"F0.imprint","INTERSECT",VERTEX,{"derivedFrom":[subQ0,sQuery(id+"F0.wireOp",EDGE,"E3")]});Q4=makeQuery(id+"F1.opExtrude","CAP_EDGE",EDGE,{"disambiguationData":[OSD([subQ0]),TDD([makeQuery(id+"F0.imprint","IMPRINT",EDGE,{"disambiguationData":[TD([[subQ1,-1.0]])],"derivedFrom":subQ0}),makeQuery(id+"F0.imprint","IMPRINT",EDGE,{"disambiguationData":[TD([[subQ1,1.0]])],"derivedFrom":subQ0})])],"isStart":false});}
            var Q5;
            {var subQ0=sQuery(id+"F0.wireOp",EDGE,"E0");var subQ1=makeQuery(id+"F0.imprint","INTERSECT",VERTEX,{"derivedFrom":[subQ0,sQuery(id+"F0.wireOp",EDGE,"E14")]});Q5=makeQuery(id+"F1.opExtrude","CAP_EDGE",EDGE,{"disambiguationData":[OSD([subQ0]),TDD([makeQuery(id+"F0.imprint","IMPRINT",EDGE,{"disambiguationData":[TD([[subQ1,1.0]])],"derivedFrom":subQ0}),makeQuery(id+"F0.imprint","IMPRINT",EDGE,{"disambiguationData":[TD([[subQ1,-1.0]])],"derivedFrom":subQ0})])],"isStart":false});}
            var Q6;
            {var subQ0=sQuery(id+"F0.wireOp",EDGE,"E0");var subQ1=makeQuery(id+"F0.imprint","INTERSECT",VERTEX,{"derivedFrom":[subQ0,sQuery(id+"F0.wireOp",EDGE,"E4")]});Q6=makeQuery(id+"F1.opExtrude","CAP_EDGE",EDGE,{"disambiguationData":[OSD([subQ0]),TDD([makeQuery(id+"F0.imprint","IMPRINT",EDGE,{"disambiguationData":[TD([[subQ1,1.0]])],"derivedFrom":subQ0}),makeQuery(id+"F0.imprint","IMPRINT",EDGE,{"disambiguationData":[TD([[subQ1,-1.0]])],"derivedFrom":subQ0})])],"isStart":false});}
            var Q7;
            {var subQ0=sQuery(id+"F0.wireOp",EDGE,"E0");var subQ1=makeQuery(id+"F0.imprint","INTERSECT",VERTEX,{"derivedFrom":[subQ0,sQuery(id+"F0.wireOp",EDGE,"E13")]});Q7=makeQuery(id+"F1.opExtrude","CAP_EDGE",EDGE,{"disambiguationData":[OSD([subQ0]),TDD([makeQuery(id+"F0.imprint","IMPRINT",EDGE,{"disambiguationData":[TD([[subQ1,1.0]])],"derivedFrom":subQ0}),makeQuery(id+"F0.imprint","IMPRINT",EDGE,{"disambiguationData":[TD([[subQ1,-1.0]])],"derivedFrom":subQ0})])],"isStart":false});}
            chamfer(context, id + "F4", {"entities" : qUnion([Q0, Q1, Q2, Q3, Q4, Q5, Q6, Q7]), "width" : 1 * mm, "tangentPropagation" : true});
        }
    });
